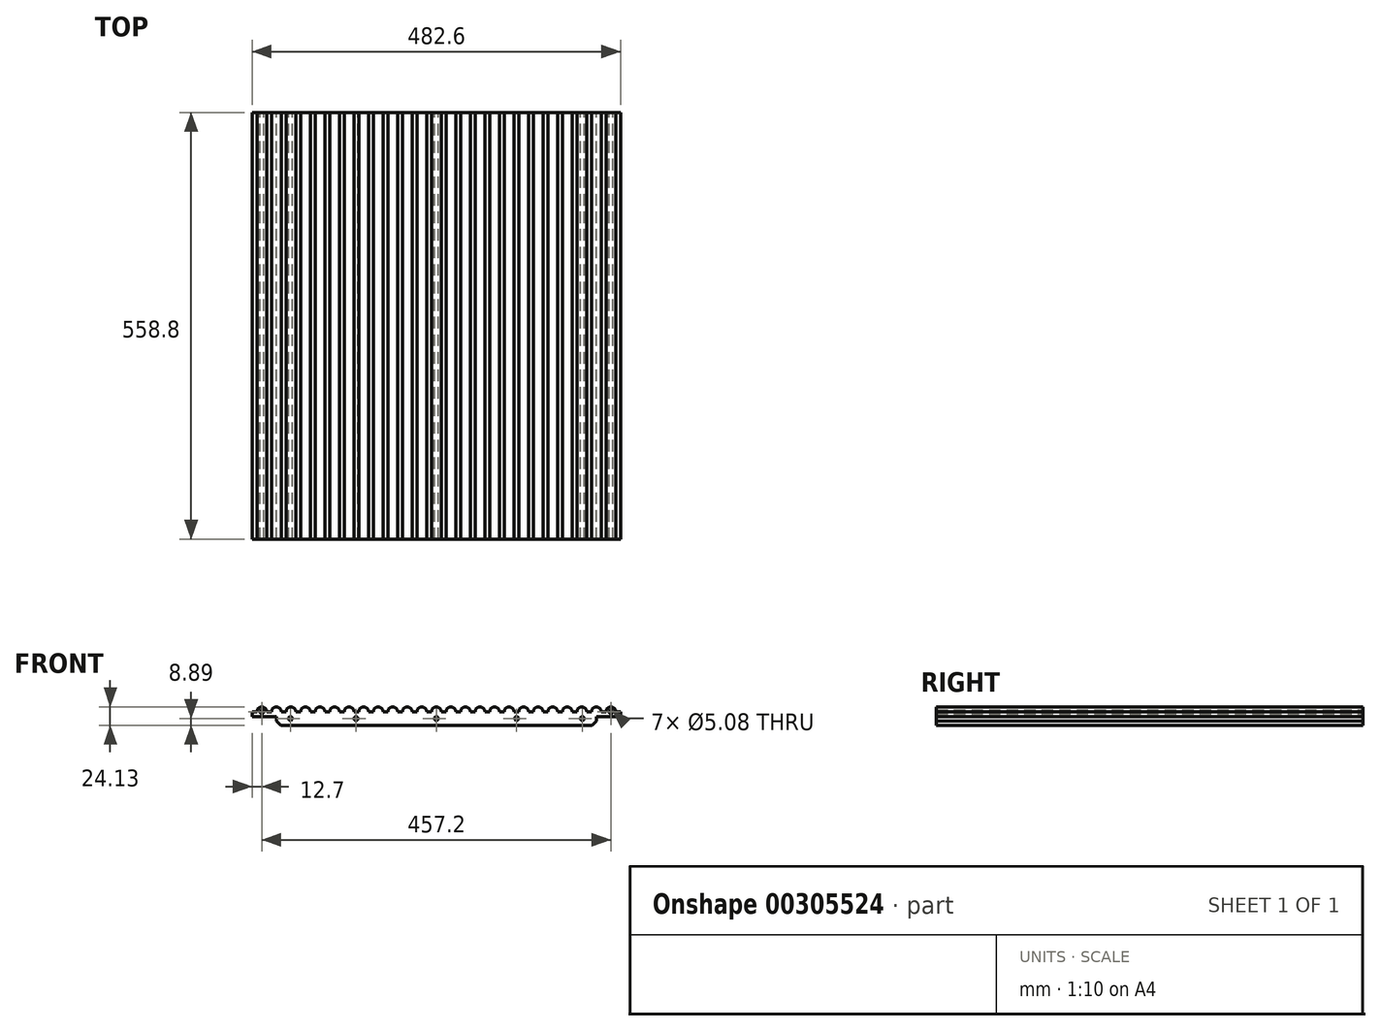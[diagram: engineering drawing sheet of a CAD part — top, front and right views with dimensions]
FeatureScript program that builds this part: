
annotation { "Feature Type Name" : "Feature", "Feature Type Description" : "" }
export const myFeature = defineFeature(function(context is Context, id is Id, definition is map)
    precondition{}
    {
        {
            var Q0;
            Q0=qCreatedBy(makeId("Front.planeOp"),FACE);
            var sketch = newSketch(context, id + "F0", { "sketchPlane" : qUnion([Q0])});
            skLineSegment(sketch, "E0.bottom", {"start": v(241.3, 8.9) * mm, "end": v(234.95, 8.9) * mm});
            skLineSegment(sketch, "E0.top", {"start": v(203.83, -8.9) * mm, "end": v(-203.83, -8.9) * mm});
            skLineSegment(sketch, "E0.left", {"start": v(241.3, 8.89) * mm, "end": v(241.3, 2.54) * mm});
            skLineSegment(sketch, "E0.right", {"start": v(-241.3, 8.89) * mm, "end": v(-241.3, 2.54) * mm});
            skPoint(sketch, "E0.middle", {"position": v(0, 0) * mm});
            skArc(sketch, "E1", {"start": v(6.35, 8.9) * mm, "mid": v(0, 15.24) * mm, "end": v(-6.35, 8.9) * mm});
            skArc(sketch, "E2.1.0.0", {"start": v(25.4, 8.9) * mm, "mid": v(19.05, 15.24) * mm, "end": v(12.7, 8.9) * mm});
            skArc(sketch, "E2.2.0.0", {"start": v(44.45, 8.9) * mm, "mid": v(38.1, 15.24) * mm, "end": v(31.75, 8.9) * mm});
            skArc(sketch, "E2.3.0.0", {"start": v(63.5, 8.9) * mm, "mid": v(57.15, 15.24) * mm, "end": v(50.8, 8.9) * mm});
            skArc(sketch, "E2.4.0.0", {"start": v(82.55, 8.9) * mm, "mid": v(76.2, 15.24) * mm, "end": v(69.85, 8.9) * mm});
            skArc(sketch, "E2.5.0.0", {"start": v(101.6, 8.9) * mm, "mid": v(95.25, 15.24) * mm, "end": v(88.9, 8.9) * mm});
            skArc(sketch, "E2.6.0.0", {"start": v(120.65, 8.9) * mm, "mid": v(114.3, 15.24) * mm, "end": v(107.95, 8.9) * mm});
            skArc(sketch, "E2.7.0.0", {"start": v(139.7, 8.9) * mm, "mid": v(133.35, 15.24) * mm, "end": v(127, 8.9) * mm});
            skArc(sketch, "E2.8.0.0", {"start": v(158.75, 8.9) * mm, "mid": v(152.4, 15.24) * mm, "end": v(146.05, 8.9) * mm});
            skArc(sketch, "E2.9.0.0", {"start": v(177.8, 8.9) * mm, "mid": v(171.45, 15.24) * mm, "end": v(165.1, 8.9) * mm});
            skArc(sketch, "E2.10.0.0", {"start": v(196.85, 8.9) * mm, "mid": v(190.5, 15.24) * mm, "end": v(184.15, 8.9) * mm});
            skArc(sketch, "E2.11.0.0", {"start": v(215.9, 8.9) * mm, "mid": v(209.55, 15.24) * mm, "end": v(203.2, 8.9) * mm});
            skArc(sketch, "E2.12.0.0", {"start": v(234.95, 8.9) * mm, "mid": v(228.6, 15.24) * mm, "end": v(222.25, 8.9) * mm});
            skLineSegment(sketch, "E2.direction1", {"start": v(6.35, 8.9) * mm, "end": v(12.7, 8.9) * mm, "construction": true});
            skArc(sketch, "E3.1.0.0", {"start": v(-12.7, 8.9) * mm, "mid": v(-19.05, 15.24) * mm, "end": v(-25.4, 8.9) * mm});
            skArc(sketch, "E3.2.0.0", {"start": v(-31.75, 8.9) * mm, "mid": v(-38.1, 15.24) * mm, "end": v(-44.45, 8.9) * mm});
            skArc(sketch, "E3.3.0.0", {"start": v(-50.8, 8.9) * mm, "mid": v(-57.15, 15.24) * mm, "end": v(-63.5, 8.9) * mm});
            skArc(sketch, "E3.4.0.0", {"start": v(-69.85, 8.9) * mm, "mid": v(-76.2, 15.24) * mm, "end": v(-82.55, 8.9) * mm});
            skArc(sketch, "E3.5.0.0", {"start": v(-88.9, 8.9) * mm, "mid": v(-95.25, 15.24) * mm, "end": v(-101.6, 8.9) * mm});
            skArc(sketch, "E3.6.0.0", {"start": v(-107.95, 8.9) * mm, "mid": v(-114.3, 15.24) * mm, "end": v(-120.65, 8.9) * mm});
            skArc(sketch, "E3.7.0.0", {"start": v(-127, 8.9) * mm, "mid": v(-133.35, 15.24) * mm, "end": v(-139.7, 8.9) * mm});
            skArc(sketch, "E3.8.0.0", {"start": v(-146.05, 8.9) * mm, "mid": v(-152.4, 15.24) * mm, "end": v(-158.75, 8.9) * mm});
            skArc(sketch, "E3.9.0.0", {"start": v(-165.1, 8.9) * mm, "mid": v(-171.45, 15.24) * mm, "end": v(-177.8, 8.9) * mm});
            skArc(sketch, "E3.10.0.0", {"start": v(-184.15, 8.89) * mm, "mid": v(-190.5, 15.24) * mm, "end": v(-196.85, 8.89) * mm});
            skArc(sketch, "E3.11.0.0", {"start": v(-203.2, 8.89) * mm, "mid": v(-209.55, 15.24) * mm, "end": v(-215.9, 8.89) * mm});
            skArc(sketch, "E3.12.0.0", {"start": v(-222.25, 8.89) * mm, "mid": v(-228.6, 15.24) * mm, "end": v(-234.95, 8.89) * mm});
            skLineSegment(sketch, "E3.direction1", {"start": v(-6.35, 8.9) * mm, "end": v(-12.7, 8.9) * mm, "construction": true});
            skLineSegment(sketch, "E4.trimOffspring", {"start": v(222.25, 8.9) * mm, "end": v(215.9, 8.9) * mm});
            skLineSegment(sketch, "E5.trimOffspring", {"start": v(184.15, 8.9) * mm, "end": v(177.8, 8.9) * mm});
            skLineSegment(sketch, "E6.trimOffspring", {"start": v(165.1, 8.9) * mm, "end": v(158.75, 8.9) * mm});
            skLineSegment(sketch, "E7.trimOffspring", {"start": v(146.05, 8.9) * mm, "end": v(139.7, 8.9) * mm});
            skLineSegment(sketch, "E8.trimOffspring", {"start": v(127, 8.9) * mm, "end": v(120.65, 8.9) * mm});
            skLineSegment(sketch, "E9.trimOffspring", {"start": v(107.95, 8.9) * mm, "end": v(101.6, 8.9) * mm});
            skLineSegment(sketch, "E10.trimOffspring", {"start": v(88.9, 8.9) * mm, "end": v(82.55, 8.9) * mm});
            skLineSegment(sketch, "E11.trimOffspring", {"start": v(69.85, 8.9) * mm, "end": v(63.5, 8.9) * mm});
            skLineSegment(sketch, "E12.trimOffspring", {"start": v(50.8, 8.9) * mm, "end": v(44.45, 8.9) * mm});
            skLineSegment(sketch, "E13.trimOffspring", {"start": v(31.75, 8.9) * mm, "end": v(25.4, 8.9) * mm});
            skLineSegment(sketch, "E14.trimOffspring", {"start": v(12.7, 8.9) * mm, "end": v(6.35, 8.9) * mm});
            skLineSegment(sketch, "E15.trimOffspring", {"start": v(-6.35, 8.9) * mm, "end": v(-12.7, 8.9) * mm});
            skLineSegment(sketch, "E16.trimOffspring", {"start": v(-25.4, 8.9) * mm, "end": v(-31.75, 8.9) * mm});
            skLineSegment(sketch, "E17.trimOffspring", {"start": v(-44.45, 8.9) * mm, "end": v(-50.8, 8.9) * mm});
            skLineSegment(sketch, "E18.trimOffspring", {"start": v(-82.55, 8.9) * mm, "end": v(-88.9, 8.9) * mm});
            skLineSegment(sketch, "E19.trimOffspring", {"start": v(-101.6, 8.9) * mm, "end": v(-107.95, 8.9) * mm});
            skLineSegment(sketch, "E20.trimOffspring", {"start": v(-120.65, 8.9) * mm, "end": v(-127, 8.9) * mm});
            skLineSegment(sketch, "E21.trimOffspring", {"start": v(-139.7, 8.9) * mm, "end": v(-146.05, 8.9) * mm});
            skLineSegment(sketch, "E22.trimOffspring", {"start": v(-158.75, 8.9) * mm, "end": v(-165.1, 8.9) * mm});
            skLineSegment(sketch, "E23.trimOffspring", {"start": v(-177.8, 8.9) * mm, "end": v(-184.15, 8.9) * mm});
            skLineSegment(sketch, "E24.trimOffspring", {"start": v(-196.85, 8.89) * mm, "end": v(-203.2, 8.89) * mm});
            skLineSegment(sketch, "E25.trimOffspring", {"start": v(-215.9, 8.89) * mm, "end": v(-222.25, 8.89) * mm});
            skLineSegment(sketch, "E26.trimOffspring", {"start": v(-234.95, 8.89) * mm, "end": v(-241.3, 8.89) * mm});
            skLineSegment(sketch, "E27", {"start": v(196.85, 8.9) * mm, "end": v(203.2, 8.9) * mm});
            skLineSegment(sketch, "E28", {"start": v(241.3, 2.54) * mm, "end": v(209.55, 2.54) * mm});
            skLineSegment(sketch, "E29", {"start": v(209.55, 2.54) * mm, "end": v(209.55, -3.17) * mm});
            skLineSegment(sketch, "E30", {"start": v(209.55, -3.17) * mm, "end": v(203.83, -8.9) * mm});
            skPoint(sketch, "E31.orphan", {"position": v(241.3, -8.9) * mm});
            skPoint(sketch, "E32.orphan", {"position": v(209.55, -8.9) * mm});
            skLineSegment(sketch, "E33.MirrorCS", {"start": v(-241.3, 2.54) * mm, "end": v(-209.55, 2.54) * mm});
            skLineSegment(sketch, "E34.MirrorCS", {"start": v(-209.55, 2.54) * mm, "end": v(-209.55, -3.17) * mm});
            skLineSegment(sketch, "E35.MirrorCS", {"start": v(-209.55, -3.17) * mm, "end": v(-203.83, -8.9) * mm});
            skPoint(sketch, "E36.orphan", {"position": v(-241.3, -8.9) * mm});
            skCircle(sketch, "E37", {"center": v(0, 0) * mm, "radius": 2.54 * mm});
            skPoint(sketch, "E38.centerSnap0", {"position": v(-114.3, 15.24) * mm});
            skCircle(sketch, "E39", {"center": v(-191.16, 0) * mm, "radius": 2.54 * mm});
            skCircle(sketch, "E40", {"center": v(-105.21, 0) * mm, "radius": 2.54 * mm});
            skLineSegment(sketch, "E41", {"start": v(-69.85, 8.9) * mm, "end": v(-63.5, 8.9) * mm});
            skCircle(sketch, "E42.MirrorC", {"center": v(105.21, 0) * mm, "radius": 2.54 * mm});
            skCircle(sketch, "E43.MirrorC", {"center": v(191.16, 0) * mm, "radius": 2.54 * mm});
            skCircle(sketch, "E44", {"center": v(228.6, 8.9) * mm, "radius": 2.54 * mm});
            skCircle(sketch, "E45.MirrorC", {"center": v(-228.6, 8.9) * mm, "radius": 2.54 * mm});
            skSolve(sketch);
        }
        {
            var Q0;
            Q0=makeQuery(id+"F0.imprint","IMPRINT",FACE,{"disambiguationData":[TD([[makeQuery(id+"F0.imprint","IMPRINT",EDGE,{"derivedFrom":sQuery(id+"F0.wireOp",EDGE,"E0.bottom")}),1.0]])]});
            extrude(context, id + "F1", {"entities" : qUnion([Q0]), "depth" : 558.8 * mm});
        }
    });
